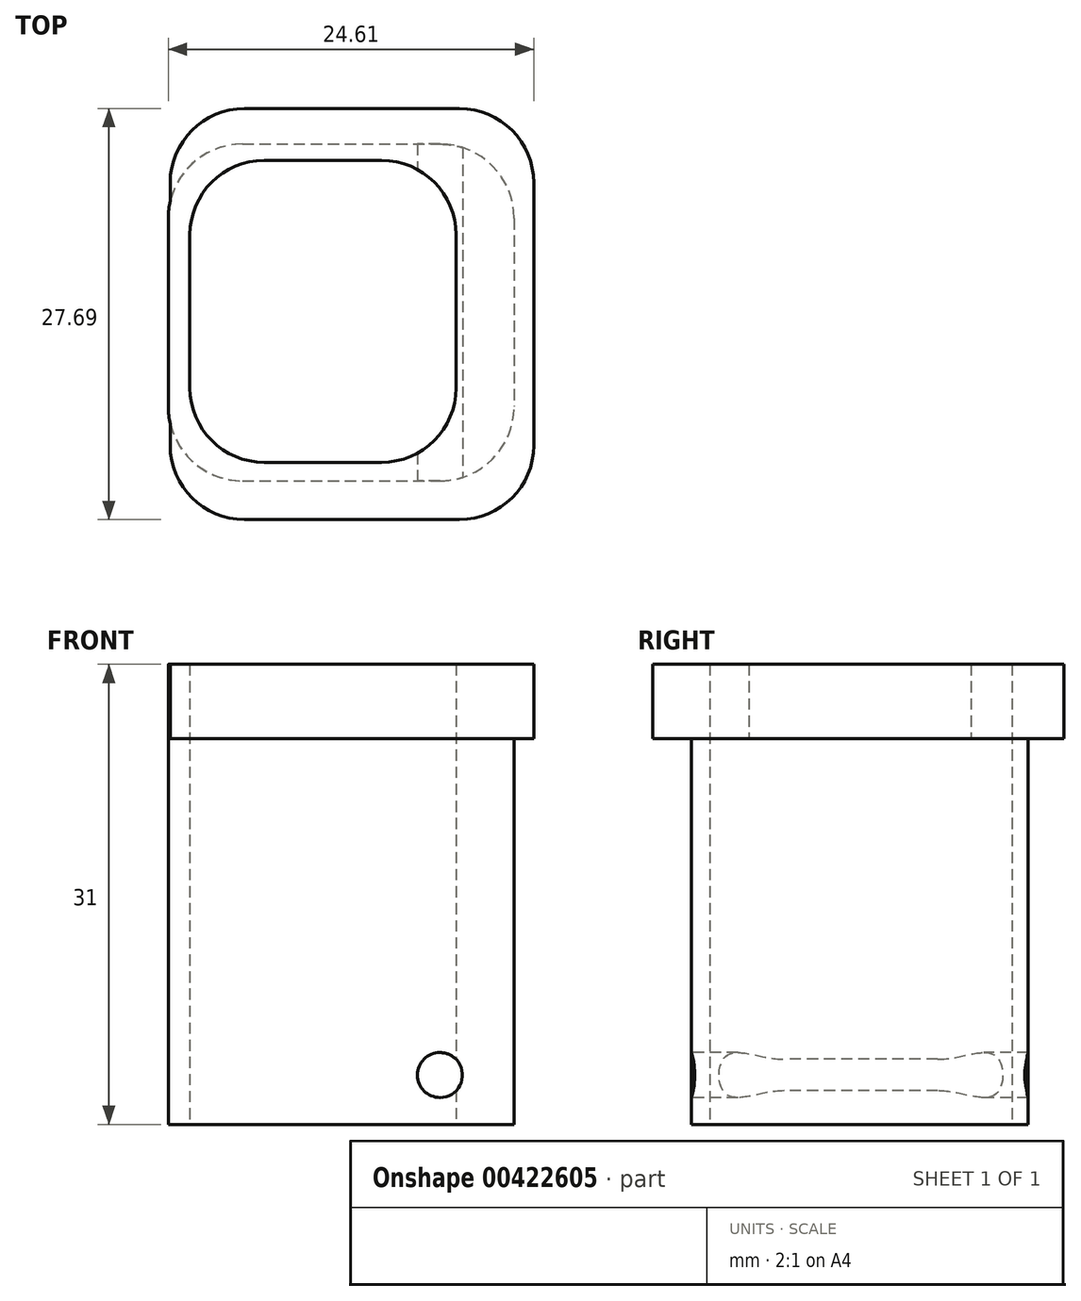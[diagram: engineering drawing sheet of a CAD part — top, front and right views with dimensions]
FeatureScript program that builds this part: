
annotation { "Feature Type Name" : "Feature", "Feature Type Description" : "" }
export const myFeature = defineFeature(function(context is Context, id is Id, definition is map)
    precondition{}
    {
        {
            var Q0;
            Q0=qCreatedBy(makeId("Top.planeOp"),FACE);
            var sketch = newSketch(context, id + "F0", { "sketchPlane" : qUnion([Q0])});
            skLineSegment(sketch, "E0.bottom", {"start": v(3.34, 10.2) * mm, "end": v(-4.57, 10.2) * mm});
            skLineSegment(sketch, "E0.top", {"start": v(3.34, -10.13) * mm, "end": v(-4.57, -10.13) * mm});
            skLineSegment(sketch, "E0.left", {"start": v(8.34, 5.2) * mm, "end": v(8.34, -5.13) * mm});
            skLineSegment(sketch, "E0.right", {"start": v(-9.57, 5.2) * mm, "end": v(-9.57, -5.13) * mm});
            skPoint(sketch, "E1.visualSharp", {"position": v(8.34, 10.2) * mm});
            skArc(sketch, "E1.filletArc", {"start": v(8.34, 5.2) * mm, "mid": v(6.88, 8.74) * mm, "end": v(3.34, 10.2) * mm});
            skPoint(sketch, "E2.visualSharp", {"position": v(-9.57, 10.2) * mm});
            skArc(sketch, "E2.filletArc", {"start": v(-4.57, 10.2) * mm, "mid": v(-8.1, 8.74) * mm, "end": v(-9.57, 5.2) * mm});
            skPoint(sketch, "E3.visualSharp", {"position": v(-9.57, -10.13) * mm});
            skArc(sketch, "E3.filletArc", {"start": v(-9.57, -5.13) * mm, "mid": v(-8.1, -8.67) * mm, "end": v(-4.57, -10.13) * mm});
            skPoint(sketch, "E4.visualSharp", {"position": v(8.34, -10.13) * mm});
            skArc(sketch, "E4.filletArc", {"start": v(3.34, -10.13) * mm, "mid": v(6.88, -8.67) * mm, "end": v(8.34, -5.13) * mm});
            skLineSegment(sketch, "E5.bottom", {"start": v(-6.03, 11.3) * mm, "end": v(7.26, 11.3) * mm});
            skLineSegment(sketch, "E5.top", {"start": v(-6.03, -11.38) * mm, "end": v(7.26, -11.38) * mm});
            skLineSegment(sketch, "E5.left", {"start": v(-11.03, 6.3) * mm, "end": v(-11.03, -6.38) * mm});
            skLineSegment(sketch, "E5.right", {"start": v(12.26, 6.3) * mm, "end": v(12.26, -6.38) * mm});
            skPoint(sketch, "E6.visualSharp", {"position": v(-11.03, 11.3) * mm});
            skArc(sketch, "E6.filletArc", {"start": v(-6.03, 11.3) * mm, "mid": v(-9.57, 9.84) * mm, "end": v(-11.03, 6.3) * mm});
            skPoint(sketch, "E7.visualSharp", {"position": v(12.26, 11.3) * mm});
            skArc(sketch, "E7.filletArc", {"start": v(12.26, 6.3) * mm, "mid": v(10.8, 9.84) * mm, "end": v(7.26, 11.3) * mm});
            skPoint(sketch, "E8.visualSharp", {"position": v(12.26, -11.38) * mm});
            skArc(sketch, "E8.filletArc", {"start": v(7.26, -11.38) * mm, "mid": v(10.8, -9.91) * mm, "end": v(12.26, -6.38) * mm});
            skPoint(sketch, "E9.visualSharp", {"position": v(-11.03, -11.38) * mm});
            skArc(sketch, "E9.filletArc", {"start": v(-11.03, -6.38) * mm, "mid": v(-9.57, -9.91) * mm, "end": v(-6.03, -11.38) * mm});
            skSolve(sketch);
        }
        {
            var Q0;
            Q0=makeQuery(id+"F0.imprint","IMPRINT",FACE,{"disambiguationData":[TD([[makeQuery(id+"F0.imprint","IMPRINT",EDGE,{"derivedFrom":sQuery(id+"F0.wireOp",EDGE,"E0.bottom")}),-1.0]])]});
            extrude(context, id + "F1", {"entities" : qUnion([Q0]), "depth" : 31 * mm});
        }
        {
            var Q0;
            Q0=makeQuery(id+"F1.opExtrude","CAP_FACE",FACE,{"disambiguationData":[OSD([sQuery(id+"F0.wireOp",EDGE,"E0.bottom"),sQuery(id+"F0.wireOp",EDGE,"E0.top"),sQuery(id+"F0.wireOp",EDGE,"E0.left"),sQuery(id+"F0.wireOp",EDGE,"E0.right"),sQuery(id+"F0.wireOp",EDGE,"E1.filletArc"),sQuery(id+"F0.wireOp",EDGE,"E2.filletArc"),sQuery(id+"F0.wireOp",EDGE,"E3.filletArc"),sQuery(id+"F0.wireOp",EDGE,"E4.filletArc"),sQuery(id+"F0.wireOp",EDGE,"E5.bottom"),sQuery(id+"F0.wireOp",EDGE,"E5.top"),sQuery(id+"F0.wireOp",EDGE,"E5.left"),sQuery(id+"F0.wireOp",EDGE,"E5.right"),sQuery(id+"F0.wireOp",EDGE,"E6.filletArc"),sQuery(id+"F0.wireOp",EDGE,"E7.filletArc"),sQuery(id+"F0.wireOp",EDGE,"E8.filletArc"),sQuery(id+"F0.wireOp",EDGE,"E9.filletArc")])],"isStart":false});
            var sketch = newSketch(context, id + "F2", { "sketchPlane" : qUnion([Q0])});
            skLineSegment(sketch, "E10.bottom", {"start": v(8.58, 13.7) * mm, "end": v(-5.9, 13.7) * mm});
            skLineSegment(sketch, "E10.top", {"start": v(8.58, -14) * mm, "end": v(-5.9, -14) * mm});
            skLineSegment(sketch, "E10.left", {"start": v(13.58, 8.7) * mm, "end": v(13.58, -9) * mm});
            skLineSegment(sketch, "E10.right", {"start": v(-10.9, 8.7) * mm, "end": v(-10.9, -9) * mm});
            skPoint(sketch, "E11.visualSharp", {"position": v(13.58, 13.7) * mm});
            skArc(sketch, "E11.filletArc", {"start": v(13.58, 8.7) * mm, "mid": v(12.11, 12.23) * mm, "end": v(8.58, 13.7) * mm});
            skPoint(sketch, "E12.visualSharp", {"position": v(13.58, -14) * mm});
            skArc(sketch, "E12.filletArc", {"start": v(8.58, -14) * mm, "mid": v(12.11, -12.53) * mm, "end": v(13.58, -9) * mm});
            skPoint(sketch, "E13.visualSharp", {"position": v(-10.9, 13.7) * mm});
            skArc(sketch, "E13.filletArc", {"start": v(-5.9, 13.7) * mm, "mid": v(-9.44, 12.23) * mm, "end": v(-10.9, 8.7) * mm});
            skPoint(sketch, "E14.visualSharp", {"position": v(-10.9, -14) * mm});
            skArc(sketch, "E14.filletArc", {"start": v(-10.9, -9) * mm, "mid": v(-9.44, -12.53) * mm, "end": v(-5.9, -14) * mm});
            skSolve(sketch);
        }
        {
            var Q0;
            Q0 = qSketchRegion(id + "F2", true);
            extrude(context, id + "F3", {"entities" : qUnion([Q0]), "operationType" : NewBodyOperationType.ADD, "oppositeDirection" : true, "depth" : 5 * mm});
        }
        {
            var Q0;
            Q0=makeQuery(id+"F2.imprint","IMPRINT",FACE,{"disambiguationData":[TD([[makeQuery(id+"F2.imprint","IMPRINT",EDGE,{"derivedFrom":makeQuery(id+"F1.opExtrude","CAP_EDGE",EDGE,{"disambiguationData":[OSD([sQuery(id+"F0.wireOp",EDGE,"E0.bottom")])],"isStart":false})}),1.0]])]});
            extrude(context, id + "F4", {"entities" : qUnion([Q0]), "operationType" : NewBodyOperationType.REMOVE, "oppositeDirection" : true, "depth" : 25 * mm});
        }
        {
            var Q0;
            Q0=makeQuery(id+"F1.opExtrude","SWEPT_FACE",FACE,{"disambiguationData":[OSD([sQuery(id+"F0.wireOp",EDGE,"E5.top")])]});
            var sketch = newSketch(context, id + "F5", { "sketchPlane" : qUnion([Q0])});
            skCircle(sketch, "E15", {"center": v(7.26, 3.32) * mm, "radius": 1.51 * mm});
            skSolve(sketch);
        }
        {
            var Q0;
            Q0 = qSketchRegion(id + "F5", true);
            extrude(context, id + "F6", {"entities" : qUnion([Q0]), "operationType" : NewBodyOperationType.REMOVE, "oppositeDirection" : true, "depth" : 25 * mm});
        }
    });
